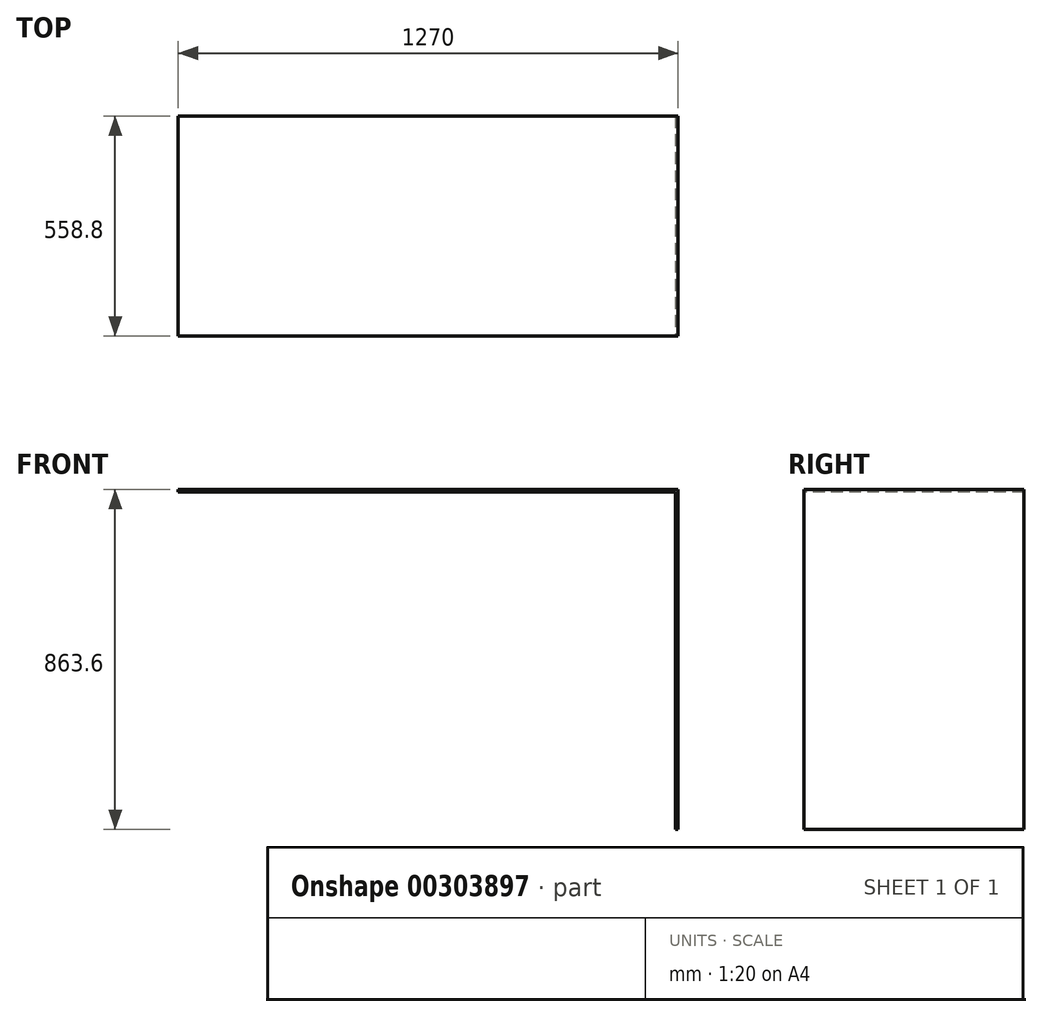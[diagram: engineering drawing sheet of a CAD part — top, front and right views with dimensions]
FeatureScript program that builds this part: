
annotation { "Feature Type Name" : "Feature", "Feature Type Description" : "" }
export const myFeature = defineFeature(function(context is Context, id is Id, definition is map)
    precondition{}
    {
        {
            var Q0;
            Q0=qCreatedBy(makeId("Front.planeOp"),FACE);
            var sketch = newSketch(context, id + "F0", { "sketchPlane" : qUnion([Q0])});
            skLineSegment(sketch, "E0", {"start": v(0, 0) * mm, "end": v(1270, 0) * mm});
            skLineSegment(sketch, "E1", {"start": v(1270, 0) * mm, "end": v(1270, -863.6) * mm});
            skLineSegment(sketch, "E2.0", {"start": v(1263.65, -6.35) * mm, "end": v(1263.65, -863.6) * mm});
            skLineSegment(sketch, "E2.1", {"start": v(0, -6.35) * mm, "end": v(1263.65, -6.35) * mm});
            skLineSegment(sketch, "E3", {"start": v(0, 0) * mm, "end": v(0, -6.35) * mm});
            skLineSegment(sketch, "E4", {"start": v(1270, -863.6) * mm, "end": v(1263.65, -863.6) * mm});
            skSolve(sketch);
        }
        {
            var Q0;
            Q0 = qSketchRegion(id + "F0", true);
            extrude(context, id + "F1", {"entities" : qUnion([Q0]), "oppositeDirection" : true, "depth" : 558.8 * mm});
        }
    });
